# Revit family: metris_single_lever_basin_mixer_100_with_pop_up_waste_set_for_hand_washbasins_31088000
name_source: partatom
category: Plumbing Fixtures
revit_build: Autodesk Revit 2015 (Build: 20140903_1530(x64)
units: mm (PartAtom-declared; Revit-internal decimal feet)

## types (1)
- Chrome 000
    BIMobject category = Taps & Mixers
    BOSUseNativeGeometries = 1
    Brand url = http://www.hansgrohe-int.com
    Default Elevation = 4' - 0"
    Design country = Germany
    EAN code = https://4011097661032
    Edition number = 1
    IFC Classification = Sanitary Terminal
    Installation instructions = https://pro.hansgrohe-int.com
    Manufacturer country = Germany
    Manufacturer name = hansgrohe
    Masterformat 2014 Code = 22 41 39
    Masterformat 2014 Description = Residential Faucets, Supplies, and Trim
    Material main = Chrome
    NBS Reference Code = 94-94-xx
    NBS Reference Description = Thermostatic Mixing Valves
    Nominal height = 0
    Nominal width = 0
    OmniClass Code = 23-31 11 19 11
    OmniClass Description = Thermostatically Controlled Faucet Mixing Valves
    Product Guid = 79d68e81-1f55-476f-9237-fd1083e65be3
    Product SKU = 31088000
    Product data url = https://bimobject.com
    Product family = Metris
    Product group = Basin mixers
    Product name = Metris Single lever basin mixer 100 with pop-up waste set for hand washbasins 31088000
    Product url = https://pro.hansgrohe-int.com
    QR code = http://bimobject.com
    Technical description = https://pro.hansgrohe-int.com
    UNSPSC Code = 301815
    Uniclass 1.4 Code = L725111
    Uniclass 1.4 Description = Mixer taps
    Uniclass 2.0 Code = PR-94-94-xx
    Uniclass 2.0 Description = Thermostatic Mixing Valves
    Uniclass 2015 Code = Pr_40_20_87_98
    Uniclass 2015 Name = Washbasin taps
    Uniformat II Code = D2010
    Uniformat II Description = Plumbing Fixtures
    Weight Net (Kg) = 0

## geometry (parser evidence)
native form markers: Sweep x2
no freeform markers — native parametric forms only
